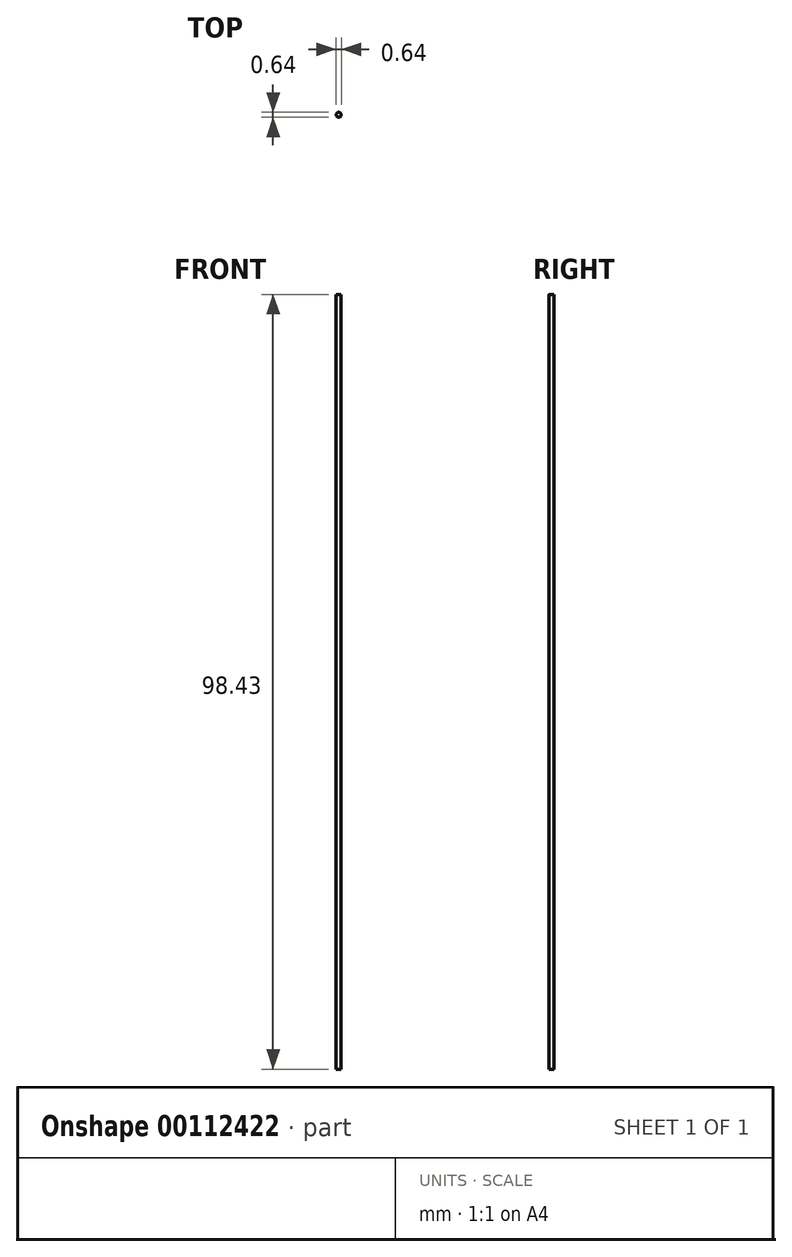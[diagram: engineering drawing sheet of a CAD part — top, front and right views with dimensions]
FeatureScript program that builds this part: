
annotation { "Feature Type Name" : "Feature", "Feature Type Description" : "" }
export const myFeature = defineFeature(function(context is Context, id is Id, definition is map)
    precondition{}
    {
        {
            var Q0;
            Q0=qCreatedBy(makeId("Top.planeOp"),FACE);
            var sketch = newSketch(context, id + "F0", { "sketchPlane" : qUnion([Q0])});
            skCircle(sketch, "E0", {"center": v(0, 0) * mm, "radius": 0.32 * mm});
            skSolve(sketch);
        }
        {
            var Q0;
            Q0 = qSketchRegion(id + "F0", true);
            extrude(context, id + "F1", {"entities" : qUnion([Q0]), "depth" : 98.42 * mm});
        }
    });
